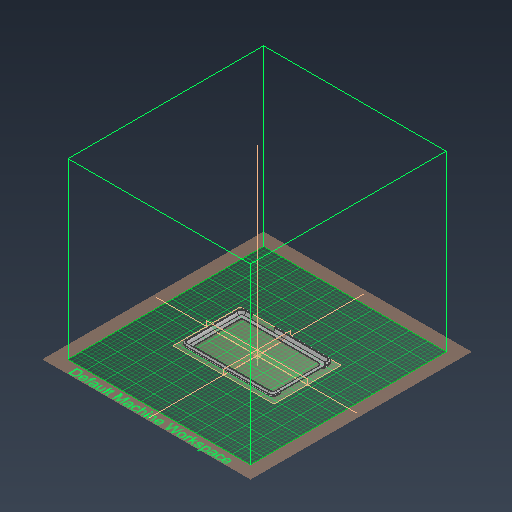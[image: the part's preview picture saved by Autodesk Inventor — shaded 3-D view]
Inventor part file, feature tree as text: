
AUTODESK INVENTOR PART (.ipt)
format: ipt  version: 2021 (Build 250183000, 183)  size: 1,596,416 bytes
history: native  units: mm
features: other x7, extrude x4, fillet x4, sketch x4, plane x2, thicken_offset x1, chamfer x1, surface_op x1
ambient origin geometry x8: Origin, YZ Plane, XZ Plane, XY Plane, X Axis, Y Axis, Z Axis, Center Point
bodies: Solid1 (feature_tree), Solid2 (feature_tree)
feature tree (24):
  extrude  "Extrusion1"  Depth=137.5mm
  fillet  "Fillet1"  [1 undecoded]
  fillet  "Fillet2"  Radius=9.9mm
  fillet  "Fillet3"  Radius=1.46mm
  thicken_offset  "Thicken1"
  chamfer  "Chamfer2"  [1 undecoded]
  extrude  "Extrusion2"  Depth=6.0mm TaperAngle=0.0deg
  plane  "Work Plane1"
  plane  "Work Plane2"
  other  "Ruled Surface6"
  surface_op  "Sculpt1"
  extrude  "Extrusion3"  Depth=6.0mm TaperAngle=0.0deg
  extrude  "Extrusion5"  Depth=5.9mm
  fillet  "Fillet5"  Radius=2.0mm
  sketch  "Sketch1"  dims[d0=208.4mm d1=137.5mm d3=0.0mm d4=9.9mm d7=1.46mm d8=0.8mm d18=0.0mm d19=0.0mm]
  sketch  "Sketch3"  dims[d20=53.5mm d22=6.0mm d23=0.0mm]
  sketch  "Sketch4"  dims[d28=5.9mm d29=6.0mm d30=0.0mm d31=5.9mm d32=2.0mm d33=2.0mm d34=3.5mm d35=10.0mm d36=3.5mm d37=10.0mm d38=5.0mm d39=0.0mm d40=5.0mm d41=10.0mm d42=8.0mm d43=8.0mm d44=8.0mm d45=8.0mm d46=5.9mm d47=24.5mm d48=19.0mm d49=19.0mm d53=0.5mm d54=2.0mm d55=45.0deg d87=10.0mm d88=5.585054mm d89=10.0mm d90=0.0mm d91=10.0mm d92=45.0deg d108=2.0mm]
  other  "Srf7"
  other  "Ruled Surface7"
  other  "Srf8"
  sketch  "3D Sketch9"
  other  "Ruled Surface8"
  other  "Srf9"
  other  "3D Intersection3"
note: 2 required parameter values undecoded (feature->parameter linkage not recoverable at this tier; creation-order binding heuristic only, values carry confidence <= 0.55)
